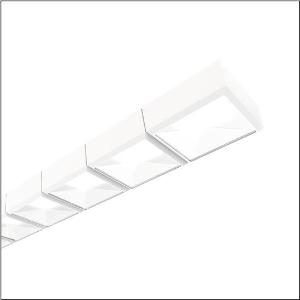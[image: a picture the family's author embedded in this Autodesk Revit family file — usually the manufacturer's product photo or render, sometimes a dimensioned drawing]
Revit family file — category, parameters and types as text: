
# Revit family: scriptus_r__11_5mz313d0twb_9c96
name_source: partatom
category: Lighting Fixtures
units: mm (PartAtom-declared; Revit-internal decimal feet)

## family parameters
Cut with Voids When Loaded = No
Host = Face
Light Source = No
Part Type = Normal
Room Calculation Point = No
Round Connector Dimension = Use Diameter
Shared = No

## types (1)
- --- (1 x LED 3000K+6500K / CRI = 80 (unbekannt), 3390 lm / 3550 lm, 3000K)
    Apparent Load = 107 VA
    CIE Flux Codes = 0 0 0 0 100 / 82 95 99 100 100
    Color Rendering = 80
    Color Temperature = 3000K
    Default Elevation = 1800 mm
    Description = Scriptus® 11, office luminaire, primary optical cover: lenses, CAT 2 (L<= 3000cd/m²), light emission: direct/indirect distribution, primary light characteristic: symmetric, installation type: suspended mounting, LED, rated luminous flux: 13.880lm, luminous efficacy: 126lm/W, light colour: 8tw, colour temperature: 3000..6500K, control gear: ECG DALI, with terminal, 5-pole, mains connection: 230V, AC, 50Hz, rated input power: 110W, LED, control gear: ECG DALI, housing, luminaire housing, of aluminium, traffic white (RAL 9016), length: 2.648mm, width: 114mm, height: 57mm, protection rating (complete): IP20, insulation class (complete): insulation class I (protective earthing), certification: CE, protection symbol: F, permissible operating ambient temperature: <= +25°C, standard: EN 50419, packaging unit: 1 piece
    Height = 57 mm
    Lamp = 1 x LED 3000K+6500K / CRI >= 80 (unbekannt)
    Lamp Light Flux = 3390 lm / 3550 lm
    Lamp count = 1
    Length = 2648 mm
    Luminous efficacy = 130 lm/W
    Manufacturer = Siteco
    ModVariant = No
    Model = 5MZ313D0TWB
    Mounting Place = Ceiling
    Mounting Type = Pendant
    Number of Poles = 1
    OnlyDefault = Yes
    Power Factor = 1
    Product Name = Scriptus® 11
    Product group = office luminaire | ceiling pendant
    ProductGroupID = 902
    Protection Class = Protection class I
    Protection Degree = IP 20
    RLX_Detail_Level = 1
    RLX_Emergency_Light_Flux = 0 lm
    RLX_Emergency_Type = 0
    RLX_Emergency_Type_DB = No
    RlxData = <blob elided: 31961 chars, md5=5e6d325a>
    Socket = socket
    Standby Power = 0 W
    System Light Flux = 13880 lm
    System Power = 107 W
    Type Comments = individual setting: colour temperature 6500K
    Type Image = l_1004839.jpg
    URL = http://relux.com
    VarID = @adj_148950
    Voltage = 0 V
    Weight = 0.00 kg
    Width = 114 mm

## geometry (parser evidence)
native form markers: Blend x4, Sweep x19
no freeform markers — native parametric forms only
